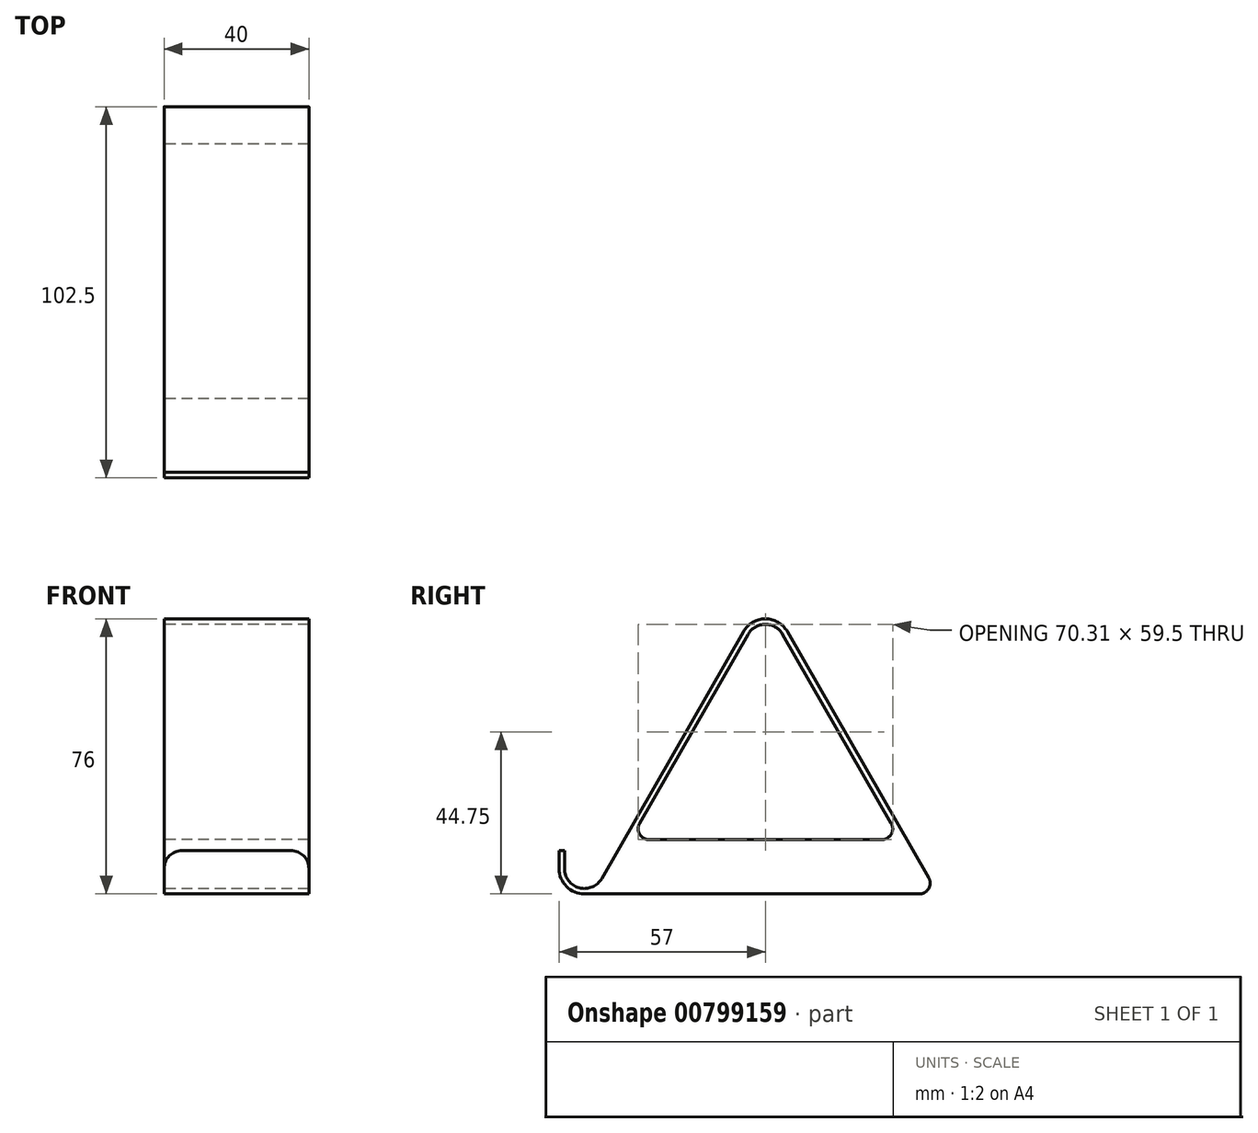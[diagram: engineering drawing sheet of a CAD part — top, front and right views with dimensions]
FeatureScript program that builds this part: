
annotation { "Feature Type Name" : "Feature", "Feature Type Description" : "" }
export const myFeature = defineFeature(function(context is Context, id is Id, definition is map)
    precondition{}
    {
        {
            var Q0;
            Q0=qCreatedBy(makeId("Right.planeOp"),FACE);
            var sketch = newSketch(context, id + "F0", { "sketchPlane" : qUnion([Q0])});
            skArc(sketch, "E0", {"start": v(-7, 0) * mm, "mid": v(-4.95, -4.95) * mm, "end": v(0, -7) * mm});
            skArc(sketch, "E1", {"start": v(54.77, 64.74) * mm, "mid": v(50, 67.5) * mm, "end": v(45.23, 64.74) * mm});
            skLineSegment(sketch, "E2", {"start": v(15.24, 12.5) * mm, "end": v(45.23, 64.74) * mm});
            skLineSegment(sketch, "E3", {"start": v(50, 62) * mm, "end": v(50, -21.9) * mm, "construction": true});
            skLineSegment(sketch, "E4", {"start": v(0, -7) * mm, "end": v(112.76, -7) * mm, "construction": true});
            skLineSegment(sketch, "E5", {"start": v(-7, 0) * mm, "end": v(-7, 5) * mm});
            skLineSegment(sketch, "E6.0", {"start": v(95.1, -2.5) * mm, "end": v(56.07, 65.48) * mm});
            skLineSegment(sketch, "E6.1", {"start": v(-5.5, 0) * mm, "end": v(-5.5, 5) * mm});
            skArc(sketch, "E6.2", {"start": v(-5.5, 0) * mm, "mid": v(-1.42, -5.31) * mm, "end": v(4.77, -2.74) * mm});
            skLineSegment(sketch, "E6.3", {"start": v(4.77, -2.74) * mm, "end": v(43.93, 65.48) * mm});
            skArc(sketch, "E6.4", {"start": v(56.07, 65.48) * mm, "mid": v(50, 69) * mm, "end": v(43.93, 65.48) * mm});
            skLineSegment(sketch, "E7", {"start": v(-7, 5) * mm, "end": v(-5.5, 5) * mm});
            skLineSegment(sketch, "E8", {"start": v(0, -7) * mm, "end": v(92.5, -7) * mm});
            skLineSegment(sketch, "E9.0", {"start": v(17.84, 8) * mm, "end": v(82.16, 8) * mm});
            skPoint(sketch, "E10.orphan", {"position": v(6.07, -3.48) * mm});
            skLineSegment(sketch, "E11.trimOffspring", {"start": v(84.76, 12.5) * mm, "end": v(54.77, 64.74) * mm});
            skPoint(sketch, "E12.visualSharp", {"position": v(12.66, 8) * mm});
            skArc(sketch, "E12.filletArc", {"start": v(15.24, 12.5) * mm, "mid": v(15.25, 9.5) * mm, "end": v(17.84, 8) * mm});
            skPoint(sketch, "E13.visualSharp", {"position": v(87.34, 8) * mm});
            skArc(sketch, "E13.filletArc", {"start": v(82.16, 8) * mm, "mid": v(84.75, 9.5) * mm, "end": v(84.76, 12.5) * mm});
            skPoint(sketch, "E14.visualSharp", {"position": v(97.68, -7) * mm});
            skArc(sketch, "E14.filletArc", {"start": v(92.5, -7) * mm, "mid": v(95.1, -5.5) * mm, "end": v(95.1, -2.5) * mm});
            skSolve(sketch);
        }
        {
            var Q0;
            Q0=makeQuery(id+"F0.imprint","IMPRINT",FACE,{"disambiguationData":[TD([[makeQuery(id+"F0.imprint","IMPRINT",EDGE,{"derivedFrom":sQuery(id+"F0.wireOp",EDGE,"E0")}),1.0]])]});
            extrude(context, id + "F1", {"entities" : qUnion([Q0]), "depth" : 40 * mm, "offsetDistance" : 25.4 * mm});
        }
        {
            var Q0;
            Q0=makeQuery(id+"F1.opExtrude","CAP_EDGE",EDGE,{"disambiguationData":[OSD([sQuery(id+"F0.wireOp",EDGE,"E7")])],"isStart":false});
            var Q1;
            Q1=makeQuery(id+"F1.opExtrude","CAP_EDGE",EDGE,{"disambiguationData":[OSD([sQuery(id+"F0.wireOp",EDGE,"E7")])],"isStart":true});
            fillet(context, id + "F2", {"entities" : qUnion([Q0, Q1]), "radius" : 5 * mm, "tangentPropagation" : true, "allowEdgeOverflow" : false});
        }
    });
